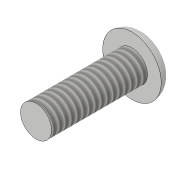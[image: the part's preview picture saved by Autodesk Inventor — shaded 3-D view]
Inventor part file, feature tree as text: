
AUTODESK INVENTOR PART (.ipt)
format: ipt  version: 2018.3 (Build 223284000, 284)  size: 104,448 bytes
history: native  units: in
note: dims shown in document units (in); Inventor stores cm internally (conversion verified against a paired STEP export)
features: extrude x2, sketch x2, fillet x1, thread x1
ambient origin geometry x8: Origin, YZ Plane, XZ Plane, XY Plane, X Axis, Y Axis, Z Axis, Center Point
bodies: Solid1 (feature_tree)
feature tree (6):
  extrude  "Extrusion1"  Depth=0.0625in TaperAngle=0.0deg
  fillet  "Fillet1"  Radius=0.0625in
  extrude  "Extrusion2"  Depth=0.5in TaperAngle=0.0deg
  thread  "Thread1"  [1 undecoded]
  sketch  "Sketch1"  dims[d0=0.305in d1=0.0625in d2=0.0in d3=0.0625in]
  sketch  "Sketch2"  dims[d4=0.162in d5=0.5in d6=0.0in d7=1.0in d8=0.0in]
note: 1 required parameter value undecoded (feature->parameter linkage not recoverable at this tier; creation-order binding heuristic only, values carry confidence <= 0.55)
